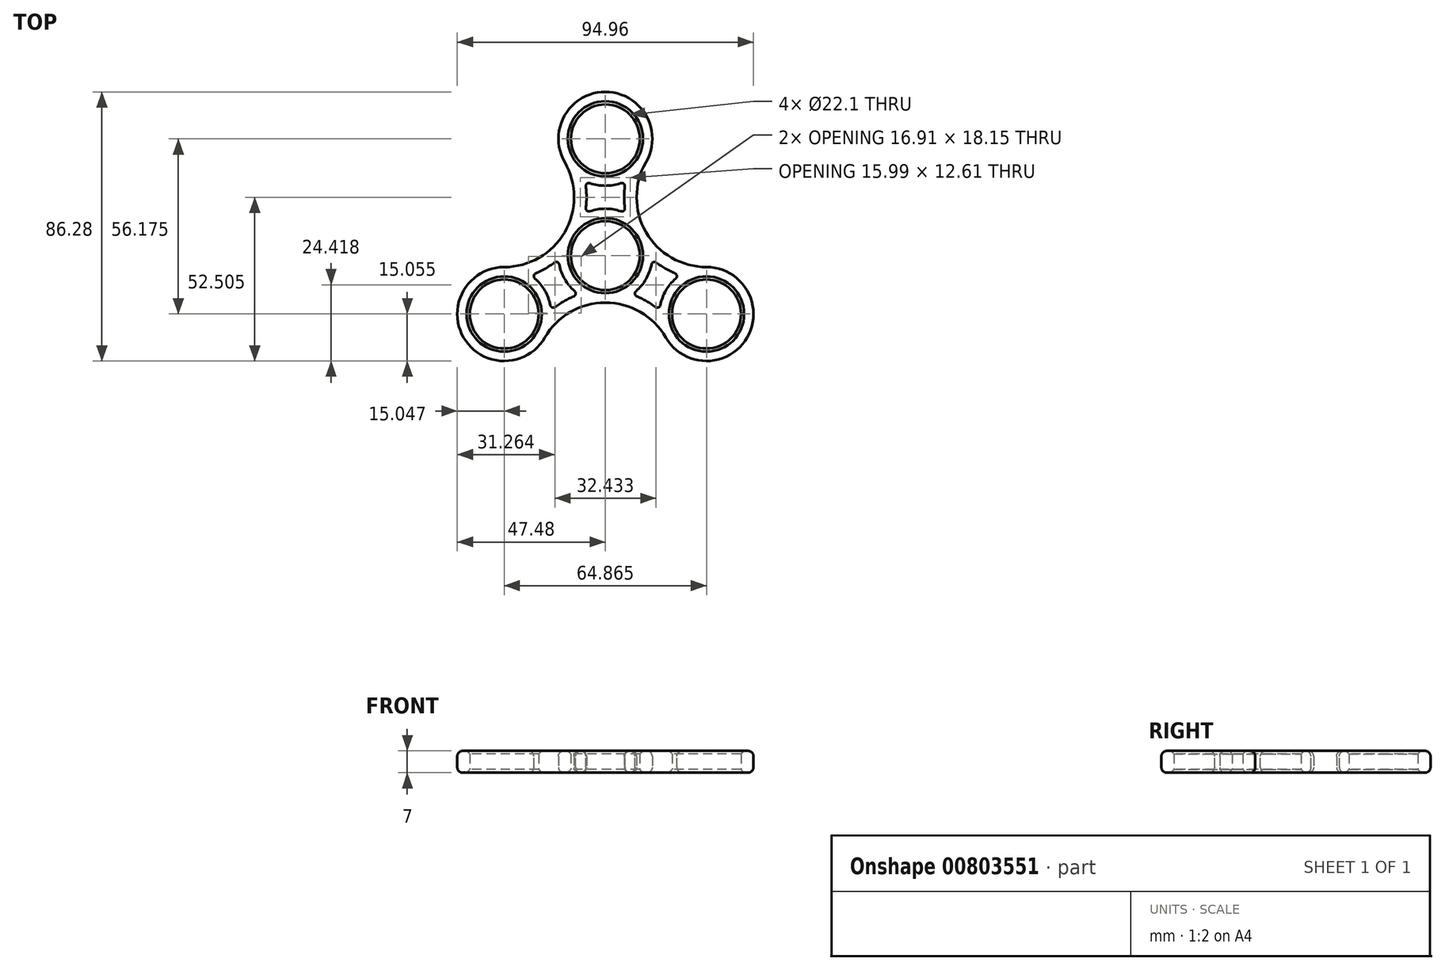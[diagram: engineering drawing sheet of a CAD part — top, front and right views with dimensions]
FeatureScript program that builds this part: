
annotation { "Feature Type Name" : "Feature", "Feature Type Description" : "" }
export const myFeature = defineFeature(function(context is Context, id is Id, definition is map)
    precondition{}
    {
        {
            var Q0;
            Q0=qCreatedBy(makeId("Top.planeOp"),FACE);
            var sketch = newSketch(context, id + "F0", { "sketchPlane" : qUnion([Q0])});
            skCircle(sketch, "E0", {"center": v(0, 0) * mm, "radius": 11.05 * mm});
            skCircle(sketch, "E1", {"center": v(0, 37.45) * mm, "radius": 11.05 * mm});
            skCircle(sketch, "E2", {"center": v(32.43, -18.72) * mm, "radius": 11.05 * mm});
            skCircle(sketch, "E3", {"center": v(-32.43, -18.72) * mm, "radius": 11.05 * mm});
            skLineSegment(sketch, "E4", {"start": v(0, 37.45) * mm, "end": v(0, 0) * mm, "construction": true});
            skLineSegment(sketch, "E5", {"start": v(32.43, -18.72) * mm, "end": v(0, 0) * mm, "construction": true});
            skLineSegment(sketch, "E6", {"start": v(-32.43, -18.72) * mm, "end": v(0, 0) * mm, "construction": true});
            skLineSegment(sketch, "E7", {"start": v(0, 37.45) * mm, "end": v(-32.43, -18.73) * mm, "construction": true});
            skLineSegment(sketch, "E8", {"start": v(-32.43, -18.72) * mm, "end": v(32.43, -18.72) * mm, "construction": true});
            skLineSegment(sketch, "E9", {"start": v(32.43, -18.72) * mm, "end": v(0, 37.45) * mm, "construction": true});
            skArc(sketch, "E10", {"start": v(6.54, 13.55) * mm, "mid": v(0, 15.05) * mm, "end": v(-6.54, 13.55) * mm});
            skArc(sketch, "E11", {"start": v(19.4, -26.25) * mm, "mid": v(45.47, -26.25) * mm, "end": v(32.43, -3.67) * mm});
            skArc(sketch, "E12", {"start": v(-32.43, -3.67) * mm, "mid": v(-45.47, -26.25) * mm, "end": v(-19.4, -26.25) * mm});
            skArc(sketch, "E13", {"start": v(-6.54, 23.9) * mm, "mid": v(0, 22.4) * mm, "end": v(6.54, 23.9) * mm});
            skArc(sketch, "E14", {"start": v(13.03, 29.92) * mm, "mid": v(13.03, 7.52) * mm, "end": v(32.43, -3.67) * mm});
            skArc(sketch, "E15", {"start": v(6.54, 23.9) * mm, "mid": v(6.03, 18.72) * mm, "end": v(6.54, 13.55) * mm});
            skArc(sketch, "E16", {"start": v(-32.43, -3.67) * mm, "mid": v(-13.03, 7.52) * mm, "end": v(-13.03, 29.92) * mm});
            skArc(sketch, "E17", {"start": v(-23.97, -6.28) * mm, "mid": v(-19.23, -4.14) * mm, "end": v(-15, -1.1) * mm});
            skArc(sketch, "E18", {"start": v(19.4, -26.25) * mm, "mid": v(0, -15.05) * mm, "end": v(-19.4, -26.25) * mm});
            skArc(sketch, "E19", {"start": v(17.42, -17.62) * mm, "mid": v(13.2, -14.59) * mm, "end": v(8.46, -12.44) * mm});
            skCircle(sketch, "E20", {"center": v(0, 0) * mm, "radius": 52.5 * mm, "construction": true});
            skArc(sketch, "E21.trimOffspring", {"start": v(13.03, 29.92) * mm, "mid": v(0, 52.5) * mm, "end": v(-13.03, 29.92) * mm});
            skArc(sketch, "E22.trimOffspring", {"start": v(15, -1.1) * mm, "mid": v(19.23, -4.14) * mm, "end": v(23.97, -6.28) * mm});
            skArc(sketch, "E23.trimOffspring", {"start": v(-6.54, 13.55) * mm, "mid": v(-6.03, 18.72) * mm, "end": v(-6.54, 23.9) * mm});
            skArc(sketch, "E24.trimOffspring", {"start": v(-15, -1.1) * mm, "mid": v(-13.03, -7.53) * mm, "end": v(-8.46, -12.44) * mm});
            skArc(sketch, "E25.trimOffspring", {"start": v(-17.42, -17.62) * mm, "mid": v(-19.4, -11.2) * mm, "end": v(-23.97, -6.28) * mm});
            skArc(sketch, "E26.trimOffspring", {"start": v(8.46, -12.44) * mm, "mid": v(13.03, -7.52) * mm, "end": v(15, -1.1) * mm});
            skArc(sketch, "E27.trimOffspring", {"start": v(-8.46, -12.44) * mm, "mid": v(-13.2, -14.59) * mm, "end": v(-17.42, -17.62) * mm});
            skArc(sketch, "E28.trimOffspring", {"start": v(23.97, -6.28) * mm, "mid": v(19.4, -11.2) * mm, "end": v(17.42, -17.62) * mm});
            skSolve(sketch);
        }
        {
            var Q0;
            Q0=makeQuery(id+"F0.imprint","IMPRINT",FACE,{"disambiguationData":[TD([[makeQuery(id+"F0.imprint","IMPRINT",EDGE,{"derivedFrom":sQuery(id+"F0.wireOp",EDGE,"E0")}),-1.0]])]});
            extrude(context, id + "F1", {"entities" : qUnion([Q0]), "depth" : 7 * mm, "offsetDistance" : 25 * mm});
        }
        {
            var Q0;
            Q0=makeQuery(id+"F1.opExtrude","SWEPT_EDGE",EDGE,{"disambiguationData":[OSD([sQuery(id+"F0.wireOp",EDGE,"E13"),sQuery(id+"F0.wireOp",EDGE,"E23.trimOffspring")])]});
            var Q1;
            Q1=makeQuery(id+"F1.opExtrude","SWEPT_EDGE",EDGE,{"disambiguationData":[OSD([sQuery(id+"F0.wireOp",EDGE,"E10"),sQuery(id+"F0.wireOp",EDGE,"E23.trimOffspring")])]});
            var Q2;
            Q2=makeQuery(id+"F1.opExtrude","SWEPT_EDGE",EDGE,{"disambiguationData":[OSD([sQuery(id+"F0.wireOp",EDGE,"E10"),sQuery(id+"F0.wireOp",EDGE,"E15")])]});
            var Q3;
            Q3=makeQuery(id+"F1.opExtrude","SWEPT_EDGE",EDGE,{"disambiguationData":[OSD([sQuery(id+"F0.wireOp",EDGE,"E13"),sQuery(id+"F0.wireOp",EDGE,"E15")])]});
            var Q4;
            Q4=makeQuery(id+"F1.opExtrude","SWEPT_EDGE",EDGE,{"disambiguationData":[OSD([sQuery(id+"F0.wireOp",EDGE,"E17"),sQuery(id+"F0.wireOp",EDGE,"E25.trimOffspring")])]});
            var Q5;
            Q5=makeQuery(id+"F1.opExtrude","SWEPT_EDGE",EDGE,{"disambiguationData":[OSD([sQuery(id+"F0.wireOp",EDGE,"E25.trimOffspring"),sQuery(id+"F0.wireOp",EDGE,"E27.trimOffspring")])]});
            var Q6;
            Q6=makeQuery(id+"F1.opExtrude","SWEPT_EDGE",EDGE,{"disambiguationData":[OSD([sQuery(id+"F0.wireOp",EDGE,"E24.trimOffspring"),sQuery(id+"F0.wireOp",EDGE,"E27.trimOffspring")])]});
            var Q7;
            Q7=makeQuery(id+"F1.opExtrude","SWEPT_EDGE",EDGE,{"disambiguationData":[OSD([sQuery(id+"F0.wireOp",EDGE,"E17"),sQuery(id+"F0.wireOp",EDGE,"E24.trimOffspring")])]});
            var Q8;
            Q8=makeQuery(id+"F1.opExtrude","SWEPT_EDGE",EDGE,{"disambiguationData":[OSD([sQuery(id+"F0.wireOp",EDGE,"E22.trimOffspring"),sQuery(id+"F0.wireOp",EDGE,"E28.trimOffspring")])]});
            var Q9;
            Q9=makeQuery(id+"F1.opExtrude","SWEPT_EDGE",EDGE,{"disambiguationData":[OSD([sQuery(id+"F0.wireOp",EDGE,"E19"),sQuery(id+"F0.wireOp",EDGE,"E28.trimOffspring")])]});
            var Q10;
            Q10=makeQuery(id+"F1.opExtrude","SWEPT_EDGE",EDGE,{"disambiguationData":[OSD([sQuery(id+"F0.wireOp",EDGE,"E19"),sQuery(id+"F0.wireOp",EDGE,"E26.trimOffspring")])]});
            var Q11;
            Q11=makeQuery(id+"F1.opExtrude","SWEPT_EDGE",EDGE,{"disambiguationData":[OSD([sQuery(id+"F0.wireOp",EDGE,"E22.trimOffspring"),sQuery(id+"F0.wireOp",EDGE,"E26.trimOffspring")])]});
            fillet(context, id + "F2", {"entities" : qUnion([Q0, Q1, Q2, Q3, Q4, Q5, Q6, Q7, Q8, Q9, Q10, Q11]), "radius" : 1 * mm, "tangentPropagation" : true, "allowEdgeOverflow" : false});
        }
        {
            var Q0;
            Q0=makeQuery(id+"F1.opExtrude","CAP_EDGE",EDGE,{"disambiguationData":[OSD([sQuery(id+"F0.wireOp",EDGE,"E16")])],"isStart":false});
            var Q1;
            Q1=makeQuery(id+"F1.opExtrude","CAP_EDGE",EDGE,{"disambiguationData":[OSD([sQuery(id+"F0.wireOp",EDGE,"E14")])],"isStart":true});
            var Q2;
            Q2=makeQuery(id+"F1.opExtrude","CAP_EDGE",EDGE,{"disambiguationData":[OSD([sQuery(id+"F0.wireOp",EDGE,"E15")])],"isStart":false});
            var Q3;
            Q3=makeQuery(id+"F1.opExtrude","CAP_EDGE",EDGE,{"disambiguationData":[OSD([sQuery(id+"F0.wireOp",EDGE,"E22.trimOffspring")])],"isStart":false});
            var Q4;
            Q4=makeQuery(id+"F1.opExtrude","CAP_EDGE",EDGE,{"disambiguationData":[OSD([sQuery(id+"F0.wireOp",EDGE,"E17")])],"isStart":false});
            var Q5;
            Q5=makeQuery(id+"F1.opExtrude","CAP_EDGE",EDGE,{"disambiguationData":[OSD([sQuery(id+"F0.wireOp",EDGE,"E24.trimOffspring")])],"isStart":true});
            var Q6;
            Q6=makeQuery(id+"F1.opExtrude","CAP_EDGE",EDGE,{"disambiguationData":[OSD([sQuery(id+"F0.wireOp",EDGE,"E10")])],"isStart":true});
            var Q7;
            Q7=makeQuery(id+"F1.opExtrude","CAP_EDGE",EDGE,{"disambiguationData":[OSD([sQuery(id+"F0.wireOp",EDGE,"E22.trimOffspring")])],"isStart":true});
            fillet(context, id + "F3", {"entities" : qUnion([Q0, Q1, Q2, Q3, Q4, Q5, Q6, Q7]), "radius" : 1.75 * mm, "tangentPropagation" : true, "allowEdgeOverflow" : false});
        }
        {
            var Q0;
            Q0=makeQuery(id+"F1.opExtrude","SWEPT_FACE",FACE,{"disambiguationData":[OSD([sQuery(id+"F0.wireOp",EDGE,"E0")])]});
            var Q1;
            Q1=makeQuery(id+"F1.opExtrude","SWEPT_FACE",FACE,{"disambiguationData":[OSD([sQuery(id+"F0.wireOp",EDGE,"E1")])]});
            var Q2;
            Q2=makeQuery(id+"F1.opExtrude","SWEPT_FACE",FACE,{"disambiguationData":[OSD([sQuery(id+"F0.wireOp",EDGE,"E2")])]});
            var Q3;
            Q3=makeQuery(id+"F1.opExtrude","SWEPT_FACE",FACE,{"disambiguationData":[OSD([sQuery(id+"F0.wireOp",EDGE,"E3")])]});
            chamfer(context, id + "F4", {"entities" : qUnion([Q0, Q1, Q2, Q3]), "width" : 1 * mm, "tangentPropagation" : true});
        }
    });
